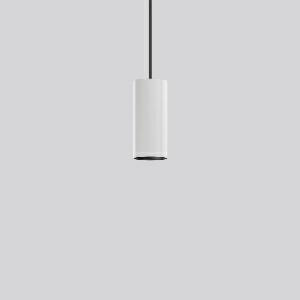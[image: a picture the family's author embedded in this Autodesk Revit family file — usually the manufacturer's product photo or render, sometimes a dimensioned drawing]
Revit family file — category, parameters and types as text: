
# Revit family: deecos_p_mini_911514_002_2_a131
name_source: partatom
category: Lighting Fixtures
units: mm (PartAtom-declared; Revit-internal decimal feet)

## family parameters
Cut with Voids When Loaded = No
Host = Face
Light Source = No
Part Type = Normal
Room Calculation Point = No
Round Connector Dimension = Use Diameter
Shared = No

## types (1)
- DEECOS P mini (1 x LED Modul 927, 2300 lm, 2700)
    Apparent Load = 20 VA
    Approval mark = CE
    CIE Flux Codes = 99 100 100 100 100
    Color Rendering = 92
    Color Temperature = 2700
    Default Elevation = 1800 mm
    Description = Series: DEECOS P mini
Cylindrical pendant luminaire. Housing: die-cast aluminium, powder-coated. Canopy made of powder-coated sheet steel with magnetic attachment. Optical assembly with reflector made of MIRO-Silver with 98% total light reflection for outstanding efficiency - can be changed without tools. Best colour rendering index Ra>90. Transparent pendant cable 5 m, can be shortened, with integrated steel cable. High quality converter without flickering and stroboscopic effect. The following accessories can be mounted without use of tools: interchangeable lenses, honeycomb louvre, clear and frosted diffusers, white interchangeable plastic ring. Decorative recessed suspension set available as accessory.Suitable for accessory Deecos P Tube cylinder extensions 0.5 m, 0.75 m or 1 m. 
Colour: traffic white, matt (RAL 9016)
Diameter: 87 mm
Height: 195 mm
Suspension length: 5000 mm
Lamp: LED
Socket: without socket
Colour temperature: 2700K
Colour rendering index (CRI): 92
System power: 20 W
Rated luminous flux: 2300 lm
Luminous efficiency: 115 lm/W
Control gear: Regulated power supply
Protection class: I
Type of protection: IP 20
    Height = 195 mm
    Lamp = 1 x LED Modul 927
    Lamp Light Flux = 2300 lm
    Lamp count = 1
    Length = 87 mm
    Lifetime = 50000 h
    Luminous efficacy = 115 lm/W
    Manufacturer = RZB
    ModVariant = No
    Model = 911514.002.2
    Mounting Place = Ceiling
    Mounting Type = Pendant
    Number of Poles = 1
    OnlyDefault = Yes
    Power Factor = 1
    Product Name = DEECOS P mini
    Product group = Pendant luminaires
    ProductGroupID = 902
    Protection Class = Protection class I
    Protection Degree = IP 20
    RLX_Detail_Level = 1
    RLX_Emergency_Light_Flux = 0 lm
    RLX_Emergency_Type = 0
    RLX_Emergency_Type_DB = No
    RlxData = <blob elided: 55113 chars, md5=a8f710c4>
    Socket = socket
    Standby Power = 0 W
    System Light Flux = 2300 lm
    System Power = 20 W
    Type Comments = Product without accessories
    Type Image = 911476.002.jpg
    URL = http://relux.com
    VarID = ---
    Voltage = 230 V
    Voltage Range = 220-240 V
    Weight = 0.00 kg
    Width = 0 mm  [stored 0 ft]

note: [stored X ft] marks values corroborated as IEEE doubles in the binary element streams (Revit-internal decimal feet)

## geometry (parser evidence)
native form markers: Blend x4, Sweep x11
no freeform markers — native parametric forms only
